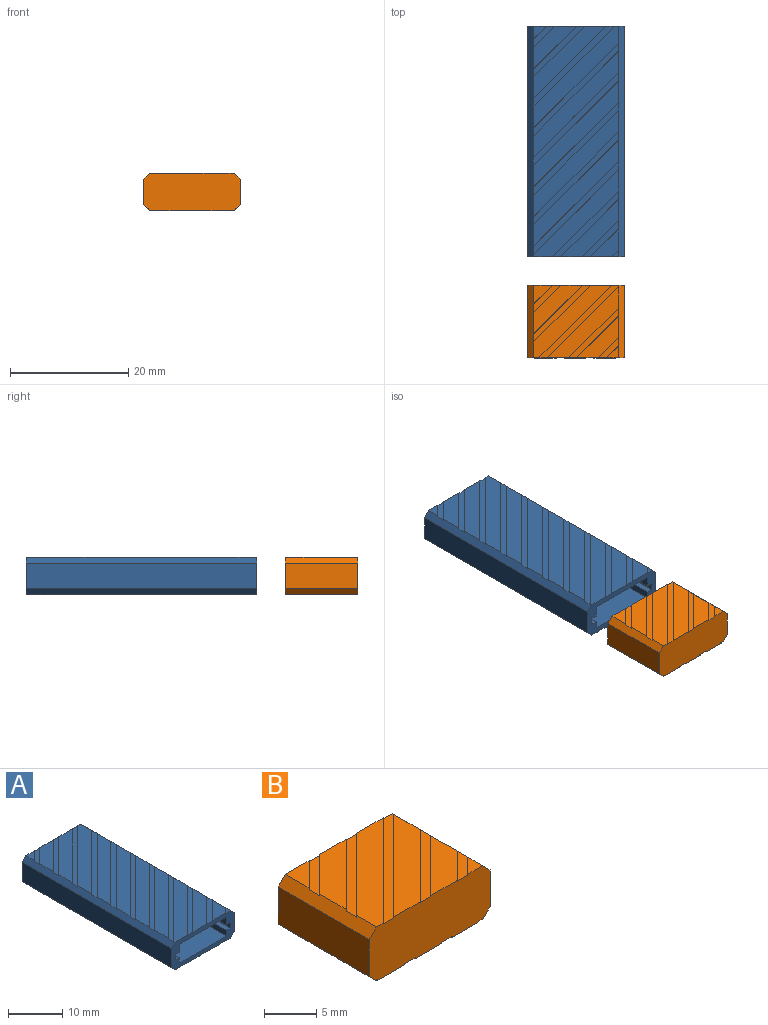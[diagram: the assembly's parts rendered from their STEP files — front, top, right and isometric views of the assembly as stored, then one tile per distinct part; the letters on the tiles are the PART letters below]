
ASSEMBLY  parts=2 mates=1
PART A: 109 faces, bbox 16.3x39x6.3 mm
  f0: plane 15.41x14.3mm, normal (0,0,-1), area 48.2mm2, adj f11,f13,f14,f98,f106
  f1: plane 10.41x10.41mm, normal (0,0,-1), area 30.9mm2, adj f11,f13,f100,f107
  f2: plane 17.89x14.3mm, normal (0,0,-1), area 51.3mm2, adj f13,f14,f91,f95
  f3: plane 17.89x14.3mm, normal (0,0,-1), area 51.3mm2, adj f13,f14,f92,f97
  f4: plane 0.41x0.41mm, normal (0,0,-1), area 0.1mm2, adj f11,f13,f103
  f5: plane 5.41x5.41mm, normal (0,0,-1), area 13mm2, adj f11,f13,f101,f104
  f6: plane 6.47x6.47mm, normal (0,0,-1), area 16.8mm2, adj f12,f14,f79,f88
  f7: plane 17.89x14.3mm, normal (0,0,-1), area 51.3mm2, adj f13,f14,f82,f86
  f8: plane 17.89x14.3mm, normal (0,0,-1), area 51.3mm2, adj f13,f14,f83,f94
  f9: plane 11.47x11.47mm, normal (0,0,-1), area 34.7mm2, adj f12,f14,f76,f80
  f10: plane 16.47x14.3mm, normal (0,0,-1), area 50.3mm2, adj f12,f13,f14,f77,f85
  f11: plane 16.3x6.31mm, normal (0,1,0), area 100mm2, adj f0,f1,f4,f5,f13,f14,f22,f23
  f12: plane 16.3x6.31mm, normal (0,-1,0), area 44.6mm2, adj f6,f9,f10,f13,f14,f19,f20,f21
  f13: plane 39x1mm, normal (0.71,0,-0.71), area 53.6mm2, adj f0,f1,f2,f3,f4,f5,f7,f8
  f14: plane 39x1mm, normal (-0.71,0,-0.71), area 53.6mm2, adj f0,f2,f3,f6,f7,f8,f9,f10
  f15: plane 17.89x14.3mm, normal (0,0,1), area 51.3mm2, adj f26,f27,f57,f65
  f16: plane 17.89x14.3mm, normal (0,0,1), area 51.3mm2, adj f26,f27,f62,f66
  f17: plane 17.89x14.3mm, normal (0,0,1), area 51.3mm2, adj f26,f27,f47,f60
  f18: plane 17.89x14.3mm, normal (0,0,1), area 51.3mm2, adj f26,f27,f56,f59
  f19: plane 4.7x4.7mm, normal (0,0,1), area 10.4mm2, adj f12,f26,f69,f74
  f20: plane 14.7x14.3mm, normal (0,0,1), area 46.2mm2, adj f12,f26,f27,f63,f71
  f21: plane 9.7x9.7mm, normal (0,0,1), area 28.4mm2, adj f12,f26,f68,f72
  f22: plane 7.19x7.19mm, normal (0,0,1), area 19.3mm2, adj f11,f27,f51,f54
  f23: plane 2.19x2.19mm, normal (0,0,1), area 2.4mm2, adj f11,f27,f50
  f24: plane 17.19x14.3mm, normal (0,0,1), area 51mm2, adj f11,f26,f27,f45,f48
  f25: plane 12.19x12.19mm, normal (0,0,1), area 37.3mm2, adj f11,f27,f44,f53
  f26: plane 39x1mm, normal (0.71,0,0.71), area 53.6mm2, adj f11,f12,f15,f16,f17,f18,f19,f20
  f27: plane 39x1mm, normal (-0.71,0,0.71), area 53.6mm2, adj f11,f12,f15,f16,f17,f18,f20,f22
  f28: plane 37.3x1.26mm, normal (1,0,0), area 46.8mm2, adj f12,f29,f42,f43
  f29: plane 37.3x1mm, normal (0,0,1), area 37.3mm2, adj f12,f28,f36,f43
  f30: plane 37.3x1mm, normal (0,0,-1), area 37.3mm2, adj f12,f31,f36,f43
  f31: plane 37.3x1.86mm, normal (1,0,0), area 69.2mm2, adj f12,f30,f37,f43
  f32: plane 37.3x1.86mm, normal (-1,0,0), area 69.2mm2, adj f12,f33,f37,f43
  f33: plane 37.3x1mm, normal (0,0,-1), area 37.3mm2, adj f12,f32,f38,f43
  f34: plane 37.3x1mm, normal (0,0,1), area 37.3mm2, adj f12,f35,f38,f43
  f35: plane 37.3x1.26mm, normal (-1,0,0), area 46.8mm2, adj f12,f34,f42,f43
  f36: plane 37.3x1.2mm, normal (1,0,0), area 44.8mm2, adj f12,f29,f30,f43
  f37: plane 37.3x12.3mm, normal (0,0,-1), area 458.8mm2, adj f12,f31,f32,f43
  f38: plane 37.3x1.2mm, normal (-1,0,0), area 44.8mm2, adj f12,f33,f34,f43
  f39: plane 39x4.31mm, normal (1,0,0), area 168.1mm2, adj f11,f12,f13,f26
  f40: plane 39x4.31mm, normal (-1,0,0), area 168.1mm2, adj f11,f12,f14,f27
  f41: plane 1.47x1.47mm, normal (0,0,-1), area 1.1mm2, adj f12,f14,f89
  f42: plane 37.3x12.3mm, normal (0,0,1), area 458.8mm2, adj f12,f28,f35,f43
  f43: plane 14.3x4.31mm, normal (0,-1,0), area 55.4mm2, adj f28,f29,f30,f31,f32,f33,f34,f35
  f44: plane 12.29x12.29mm, normal (0.71,-0.71,0), area 1.7mm2, adj f11,f25,f27,f46
  f45: plane 13.7x13.7mm, normal (-0.71,0.71,0), area 1.9mm2, adj f11,f24,f27,f46
  f46: plane 13.7x13.7mm, normal (0,0,1), area 18.4mm2, adj f11,f27,f44,f45
  f47: plane 14.5x14.5mm, normal (-0.71,0.71,0), area 2mm2, adj f17,f26,f27,f49
  f48: plane 14.5x14.5mm, normal (0.71,-0.71,0), area 2mm2, adj f24,f26,f27,f49
  f49: plane 15.91x14.5mm, normal (0,0,1), area 20.5mm2, adj f26,f27,f47,f48
  f50: plane 2.29x2.29mm, normal (0.71,-0.71,0), area 0.3mm2, adj f11,f23,f27,f52
  f51: plane 3.7x3.7mm, normal (-0.71,0.71,0), area 0.5mm2, adj f11,f22,f27,f52
  f52: plane 3.7x3.7mm, normal (0,0,1), area 4.2mm2, adj f11,f27,f50,f51
  f53: plane 8.7x8.7mm, normal (-0.71,0.71,0), area 1.2mm2, adj f11,f25,f27,f55
  f54: plane 7.29x7.29mm, normal (0.71,-0.71,0), area 1mm2, adj f11,f22,f27,f55
  f55: plane 8.7x8.7mm, normal (0,0,1), area 11.3mm2, adj f11,f27,f53,f54
  f56: plane 14.5x14.5mm, normal (0.71,-0.71,0), area 2mm2, adj f18,f26,f27,f58
  f57: plane 14.5x14.5mm, normal (-0.71,0.71,0), area 2mm2, adj f15,f26,f27,f58
  f58: plane 15.91x14.5mm, normal (0,0,1), area 20.5mm2, adj f26,f27,f56,f57
  f59: plane 14.5x14.5mm, normal (-0.71,0.71,0), area 2mm2, adj f18,f26,f27,f61
  f60: plane 14.5x14.5mm, normal (0.71,-0.71,0), area 2mm2, adj f17,f26,f27,f61
  f61: plane 15.91x14.5mm, normal (0,0,1), area 20.5mm2, adj f26,f27,f59,f60
  f62: plane 14.5x14.5mm, normal (0.71,-0.71,0), area 2mm2, adj f16,f26,f27,f64
  f63: plane 14.5x14.5mm, normal (-0.71,0.71,0), area 2mm2, adj f20,f26,f27,f64
  f64: plane 15.91x14.5mm, normal (0,0,1), area 20.5mm2, adj f26,f27,f62,f63
  f65: plane 14.5x14.5mm, normal (0.71,-0.71,0), area 2mm2, adj f15,f26,f27,f67
  f66: plane 14.5x14.5mm, normal (-0.71,0.71,0), area 2mm2, adj f16,f26,f27,f67
  f67: plane 15.91x14.5mm, normal (0,0,1), area 20.5mm2, adj f26,f27,f65,f66
  f68: plane 6.21x6.21mm, normal (0.71,-0.71,0), area 0.9mm2, adj f12,f21,f26,f70
  f69: plane 4.8x4.8mm, normal (-0.71,0.71,0), area 0.7mm2, adj f12,f19,f26,f70
  f70: plane 6.21x6.21mm, normal (0,0,1), area 7.8mm2, adj f12,f26,f68,f69
  f71: plane 11.21x11.21mm, normal (0.71,-0.71,0), area 1.6mm2, adj f12,f20,f26,f73
  f72: plane 9.8x9.8mm, normal (-0.71,0.71,0), area 1.4mm2, adj f12,f21,f26,f73
  f73: plane 11.21x11.21mm, normal (0,0,1), area 14.9mm2, adj f12,f26,f71,f72
  f74: plane 1.21x1.21mm, normal (0.71,-0.71,0), area 0.2mm2, adj f12,f19,f26,f75
  f75: plane 1.21x1.21mm, normal (0,0,1), area 0.7mm2, adj f12,f26,f74
  f76: plane 11.57x11.57mm, normal (0.71,0.71,0), area 1.6mm2, adj f9,f12,f14,f78
  f77: plane 12.99x12.99mm, normal (-0.71,-0.71,0), area 1.8mm2, adj f10,f12,f14,f78
  f78: plane 12.99x12.99mm, normal (0,0,-1), area 17.4mm2, adj f12,f14,f76,f77
  f79: plane 6.57x6.57mm, normal (0.71,0.71,0), area 0.9mm2, adj f6,f12,f14,f81
  f80: plane 7.99x7.99mm, normal (-0.71,-0.71,0), area 1.1mm2, adj f9,f12,f14,f81
  f81: plane 7.99x7.99mm, normal (0,0,-1), area 10.3mm2, adj f12,f14,f79,f80
  f82: plane 14.5x14.5mm, normal (0.71,0.71,0), area 2mm2, adj f7,f13,f14,f84
  f83: plane 14.5x14.5mm, normal (-0.71,-0.71,0), area 2mm2, adj f8,f13,f14,f84
  f84: plane 15.91x14.5mm, normal (0,0,-1), area 20.5mm2, adj f13,f14,f82,f83
  f85: plane 14.5x14.5mm, normal (0.71,0.71,0), area 2mm2, adj f10,f13,f14,f87
  f86: plane 14.5x14.5mm, normal (-0.71,-0.71,0), area 2mm2, adj f7,f13,f14,f87
  f87: plane 15.91x14.5mm, normal (0,0,-1), area 20.5mm2, adj f13,f14,f85,f86
  f88: plane 2.99x2.99mm, normal (-0.71,-0.71,0), area 0.4mm2, adj f6,f12,f14,f90
  f89: plane 1.57x1.57mm, normal (0.71,0.71,0), area 0.2mm2, adj f12,f14,f41,f90
  f90: plane 2.99x2.99mm, normal (0,0,-1), area 3.2mm2, adj f12,f14,f88,f89
  f91: plane 14.5x14.5mm, normal (0.71,0.71,0), area 2mm2, adj f2,f13,f14,f93
  f92: plane 14.5x14.5mm, normal (-0.71,-0.71,0), area 2mm2, adj f3,f13,f14,f93
  f93: plane 15.91x14.5mm, normal (0,0,-1), area 20.5mm2, adj f13,f14,f91,f92
  f94: plane 14.5x14.5mm, normal (0.71,0.71,0), area 2mm2, adj f8,f13,f14,f96
  f95: plane 14.5x14.5mm, normal (-0.71,-0.71,0), area 2mm2, adj f2,f13,f14,f96
  f96: plane 15.91x14.5mm, normal (0,0,-1), area 20.5mm2, adj f13,f14,f94,f95
  f97: plane 14.5x14.5mm, normal (0.71,0.71,0), area 2mm2, adj f3,f13,f14,f99
  f98: plane 14.5x14.5mm, normal (-0.71,-0.71,0), area 2mm2, adj f0,f13,f14,f99
  f99: plane 15.91x14.5mm, normal (0,0,-1), area 20.5mm2, adj f13,f14,f97,f98
  f100: plane 6.93x6.93mm, normal (0.71,0.71,0), area 1mm2, adj f1,f11,f13,f102
  f101: plane 5.51x5.51mm, normal (-0.71,-0.71,0), area 0.8mm2, adj f5,f11,f13,f102
  f102: plane 6.93x6.93mm, normal (0,0,-1), area 8.8mm2, adj f11,f13,f100,f101
  f103: plane 0.51x0.51mm, normal (-0.71,-0.71,0), area 0.1mm2, adj f4,f11,f13,f105
  f104: plane 1.93x1.93mm, normal (0.71,0.71,0), area 0.3mm2, adj f5,f11,f13,f105
  f105: plane 1.93x1.93mm, normal (0,0,-1), area 1.7mm2, adj f11,f13,f103,f104
  f106: plane 11.93x11.93mm, normal (0.71,0.71,0), area 1.7mm2, adj f0,f11,f13,f108
  f107: plane 10.51x10.51mm, normal (-0.71,-0.71,0), area 1.5mm2, adj f1,f11,f13,f108
  f108: plane 11.93x11.93mm, normal (0,0,-1), area 15.9mm2, adj f11,f13,f106,f107
PART B: 57 faces, bbox 16.3x12.3x6.3 mm
  f0: plane 8.77x8.77mm, normal (0,0,-1), area 25mm2, adj f6,f9,f40,f49
  f1: plane 3.77x3.77mm, normal (0,0,-1), area 7.1mm2, adj f6,f9,f46,f48
  f2: plane 11.41x11.41mm, normal (0,0,-1), area 34.5mm2, adj f7,f8,f43,f54
  f3: plane 6.41x6.41mm, normal (0,0,-1), area 16.6mm2, adj f7,f8,f51,f55
  f4: plane 1.41x1.41mm, normal (0,0,-1), area 1mm2, adj f7,f8,f52
  f5: plane 13.77x12.3mm, normal (0,0,-1), area 41.9mm2, adj f6,f8,f9,f41,f44
  f6: plane 12.3x1mm, normal (-0.71,0,-0.71), area 17mm2, adj f0,f1,f5,f8,f9,f19,f40,f41
  f7: plane 12.3x1mm, normal (0.71,0,-0.71), area 16.9mm2, adj f2,f3,f4,f8,f9,f16,f43,f45
  f8: plane 16.3x6.31mm, normal (0,1,0), area 47mm2, adj f2,f3,f4,f5,f6,f7,f10,f12
  f9: plane 16.3x6.31mm, normal (0,-1,0), area 100.1mm2, adj f0,f1,f5,f6,f7,f10,f11,f14
  f10: plane 13.19x12.3mm, normal (0,0,1), area 40.5mm2, adj f8,f9,f18,f31,f35
  f11: plane 12x12mm, normal (0,0,1), area 36.6mm2, adj f9,f15,f28,f32
  f12: plane 3.19x3.19mm, normal (0,0,1), area 5.1mm2, adj f8,f18,f37
  f13: plane 8.19x8.19mm, normal (0,0,1), area 22.9mm2, adj f8,f18,f34,f38
  f14: plane 7x7mm, normal (0,0,1), area 18.7mm2, adj f9,f15,f25,f29
  f15: plane 12.3x1mm, normal (0.71,0,0.71), area 17mm2, adj f8,f9,f11,f14,f16,f17,f25,f26
  f16: plane 12.3x4.31mm, normal (1,0,0), area 53mm2, adj f7,f8,f9,f15
  f17: plane 2x2mm, normal (0,0,1), area 2mm2, adj f9,f15,f26
  f18: plane 12.3x1mm, normal (-0.71,0,0.71), area 17mm2, adj f8,f9,f10,f12,f13,f19,f34,f35
  f19: plane 12.3x4.31mm, normal (-1,0,0), area 53mm2, adj f6,f8,f9,f18
  f20: plane 10.6x4.31mm, normal (1,0,0), area 45.7mm2, adj f8,f21,f23,f24
  f21: plane 12.3x10.6mm, normal (0,0,-1), area 130.4mm2, adj f8,f20,f22,f24
  f22: plane 10.6x4.31mm, normal (-1,0,0), area 45.7mm2, adj f8,f21,f23,f24
  f23: plane 12.3x10.6mm, normal (0,0,1), area 130.4mm2, adj f8,f20,f22,f24
  f24: plane 12.3x4.31mm, normal (0,1,0), area 53mm2, adj f20,f21,f22,f23
  f25: plane 3.51x3.51mm, normal (0.71,-0.71,0), area 0.5mm2, adj f9,f14,f15,f27
  f26: plane 2.1x2.1mm, normal (-0.71,0.71,0), area 0.3mm2, adj f9,f15,f17,f27
  f27: plane 3.51x3.51mm, normal (0,0,1), area 4mm2, adj f9,f15,f25,f26
  f28: plane 8.51x8.51mm, normal (0.71,-0.71,0), area 1.2mm2, adj f9,f11,f15,f30
  f29: plane 7.1x7.1mm, normal (-0.71,0.71,0), area 1mm2, adj f9,f14,f15,f30
  f30: plane 8.51x8.51mm, normal (0,0,1), area 11mm2, adj f9,f15,f28,f29
  f31: plane 12.3x12.3mm, normal (0.71,-0.71,0), area 1.7mm2, adj f8,f9,f10,f33
  f32: plane 12.1x12.1mm, normal (-0.71,0.71,0), area 1.7mm2, adj f9,f11,f15,f33
  f33: plane 13.51x12.3mm, normal (0,0,1), area 17.4mm2, adj f8,f9,f15,f31,f32
  f34: plane 8.29x8.29mm, normal (0.71,-0.71,0), area 1.2mm2, adj f8,f13,f18,f36
  f35: plane 9.7x9.7mm, normal (-0.71,0.71,0), area 1.4mm2, adj f8,f10,f18,f36
  f36: plane 9.7x9.7mm, normal (0,0,1), area 12.7mm2, adj f8,f18,f34,f35
  f37: plane 3.29x3.29mm, normal (0.71,-0.71,0), area 0.5mm2, adj f8,f12,f18,f39
  f38: plane 4.7x4.7mm, normal (-0.71,0.71,0), area 0.7mm2, adj f8,f13,f18,f39
  f39: plane 4.7x4.7mm, normal (0,0,1), area 5.6mm2, adj f8,f18,f37,f38
  f40: plane 8.87x8.87mm, normal (0.71,0.71,0), area 1.2mm2, adj f0,f6,f9,f42
  f41: plane 10.29x10.29mm, normal (-0.71,-0.71,0), area 1.4mm2, adj f5,f6,f9,f42
  f42: plane 10.29x10.29mm, normal (0,0,-1), area 13.6mm2, adj f6,f9,f40,f41
  f43: plane 11.51x11.51mm, normal (-0.71,-0.71,0), area 1.6mm2, adj f2,f7,f8,f45
  f44: plane 12.3x12.3mm, normal (0.71,0.71,0), area 1.7mm2, adj f5,f8,f9,f45
  f45: plane 12.93x12.3mm, normal (0,0,-1), area 17.1mm2, adj f7,f8,f9,f43,f44
  f46: plane 0.29x0.29mm, normal (-0.71,-0.71,0), area 0mm2, adj f1,f6,f9,f47
  f47: plane 0.29x0.29mm, normal (0,0,-1), area 0mm2, adj f6,f9,f46
  f48: plane 3.87x3.87mm, normal (0.71,0.71,0), area 0.5mm2, adj f1,f6,f9,f50
  f49: plane 5.29x5.29mm, normal (-0.71,-0.71,0), area 0.7mm2, adj f0,f6,f9,f50
  f50: plane 5.29x5.29mm, normal (0,0,-1), area 6.5mm2, adj f6,f9,f48,f49
  f51: plane 2.93x2.93mm, normal (0.71,0.71,0), area 0.4mm2, adj f3,f7,f8,f53
  f52: plane 1.51x1.51mm, normal (-0.71,-0.71,0), area 0.2mm2, adj f4,f7,f8,f53
  f53: plane 2.93x2.93mm, normal (0,0,-1), area 3.1mm2, adj f7,f8,f51,f52
  f54: plane 7.93x7.93mm, normal (0.71,0.71,0), area 1.1mm2, adj f2,f7,f8,f56
  f55: plane 6.51x6.51mm, normal (-0.71,-0.71,0), area 0.9mm2, adj f3,f7,f8,f56
  f56: plane 7.93x7.93mm, normal (0,0,-1), area 10.2mm2, adj f7,f8,f54,f55
PLACE A t=(10.36,49.62,8.62)mm fixed
PLACE B t=(10.36,44.82,8.64)mm
MATE slider B.f8 <-> A.f12  axis (0,1,0) through (10.35,5.82,8.64)mm
